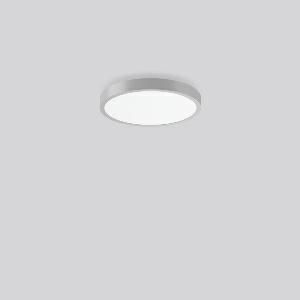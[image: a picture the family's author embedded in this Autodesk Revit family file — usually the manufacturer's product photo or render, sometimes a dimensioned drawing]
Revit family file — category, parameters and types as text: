
# Revit family: triona_round_a_312419_004_76_0175
name_source: partatom
category: Lighting Fixtures
units: mm (PartAtom-declared; Revit-internal decimal feet)

## family parameters
Cut with Voids When Loaded = No
Host = Face
Light Source = No
Part Type = Normal
Room Calculation Point = No
Round Connector Dimension = Use Diameter
Shared = No

## types (1)
- TRIONA round A (1 x LED Modul 830, 4650 lm, 3000)
    Apparent Load = 48 VA
    CIE Flux Codes = 49 80 96 100 100
    Color Rendering = 80
    Color Temperature = 3000
    Default Elevation = 1800 mm
    Description = Series: TRIONA round
Decorative round LED surface-mounted luminaire. Flat, seamless frame: aluminium extrusion profile, powder coated. Cover made of sheet steel, powder-coated. Light emission through a diffuser: plastic, opal. Lightguide and diffuser made of non-yellowing plastic (PMMA). Lateral light emission (RZB SIDELITE technology) for above-average homogeneous light distribution. Suitable for Ceiling mounting, Wall (surface). Tool-free mounting via bayonet connection. Electronic ballast included. Very easy installation thanks to Plug+Play connection. 
Colour: silver, matt (approx. RAL 9006)
Diameter: 461 mm
Height: 88 mm
Lamp: LED
Socket: without socket
Colour temperature: 3000K
Colour rendering index (CRI): 80
System power: 48 W
Rated luminous flux: 4650 lm
Luminous efficiency: 97 lm/W
Control gear: Converter, dimmable, DALI
Protection class: I
Type of protection: IP 20
    Height = 88 mm
    Lamp = 1 x LED Modul 830
    Lamp Light Flux = 4650 lm
    Lamp count = 1
    Length = 461 mm
    Lifetime = 50000 h
    Luminous efficacy = 97 lm/W
    Manufacturer = RZB
    ModVariant = No
    Model = 312419.004.76
    Mounting Place = Ceiling
    Mounting Type = Surface mounted
    Number of Poles = 1
    OnlyDefault = Yes
    Power Factor = 1
    Product Name = TRIONA round A
    Product group = Surface mounted modular luminaires
    ProductGroupID = 306
    Protection Class = Protection class I
    Protection Degree = IP 20
    RLX_Detail_Level = 1
    RLX_Emergency_Light_Flux = 0 lm
    RLX_Emergency_Type = 0
    RLX_Emergency_Type_DB = No
    RlxData = <blob elided: 27561 chars, md5=76783801>
    Socket = socket
    Standby Power = 0 W
    System Light Flux = 4650 lm
    System Power = 48 W
    Type Comments = Product without accessories
    Type Image = 312420.004.jpg
    URL = http://relux.com
    VarID = ---
    Voltage = 230 V
    Voltage Range = 220-240 V
    Weight = 0.00 kg
    Width = 0 mm  [stored 0 ft]

note: [stored X ft] marks values corroborated as IEEE doubles in the binary element streams (Revit-internal decimal feet)

## geometry (parser evidence)
native form markers: Blend x4, Sweep x10
no freeform markers — native parametric forms only
